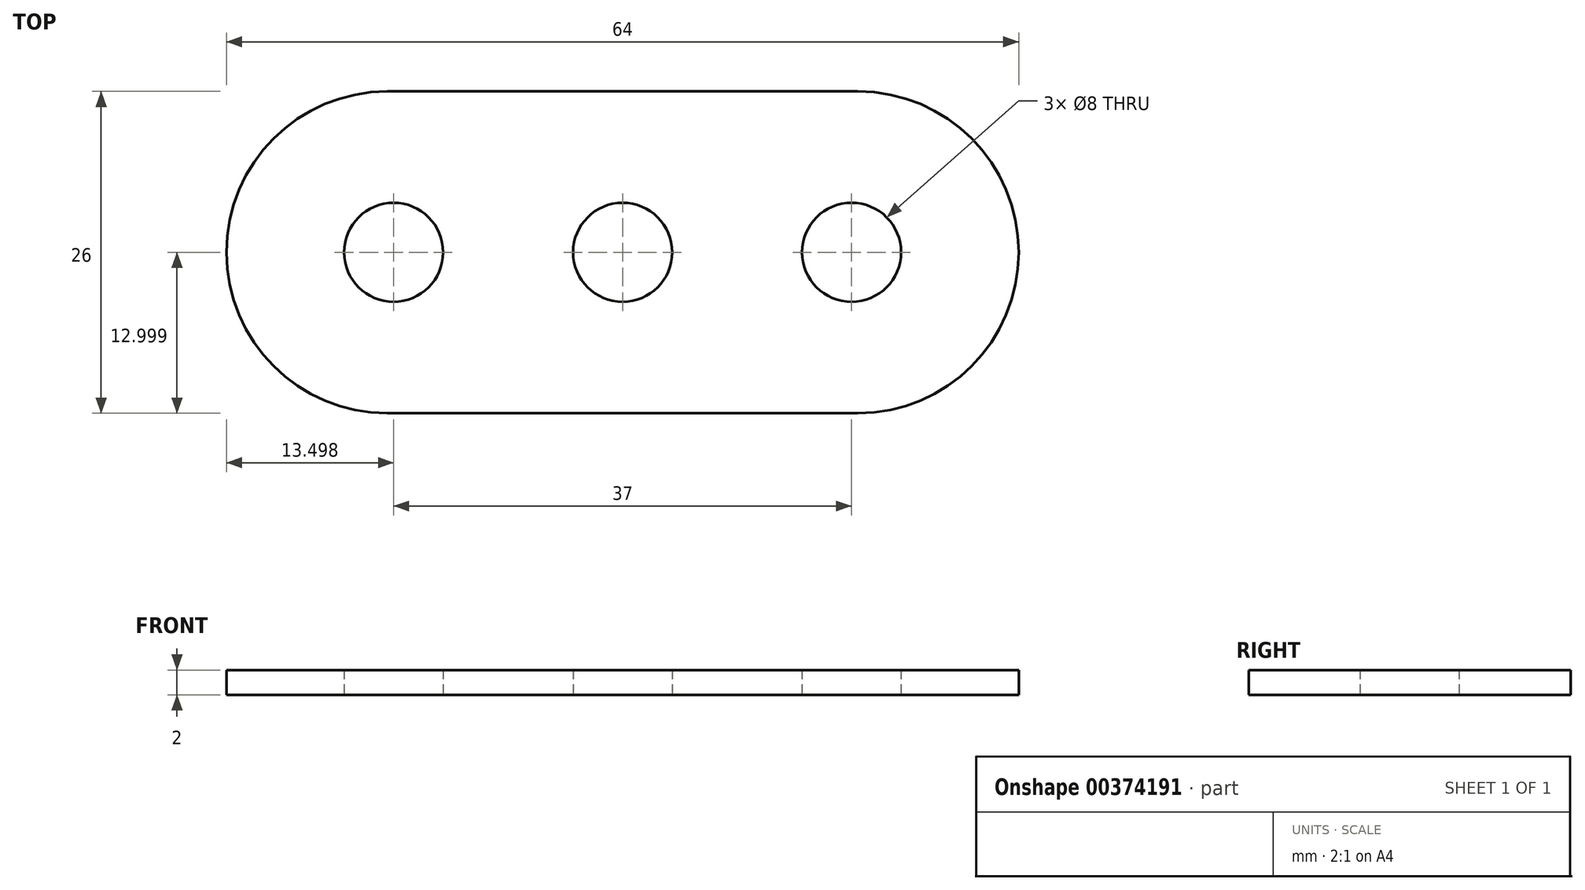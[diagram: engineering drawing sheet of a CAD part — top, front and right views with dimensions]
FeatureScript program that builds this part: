
annotation { "Feature Type Name" : "Feature", "Feature Type Description" : "" }
export const myFeature = defineFeature(function(context is Context, id is Id, definition is map)
    precondition{}
    {
        {
            var Q0;
            Q0=qCreatedBy(makeId("Top.planeOp"),FACE);
            var sketch = newSketch(context, id + "F0", { "sketchPlane" : qUnion([Q0])});
            skLineSegment(sketch, "E0.bottom", {"start": v(-21.9, 11.84) * mm, "end": v(16.1, 11.84) * mm});
            skLineSegment(sketch, "E0.top", {"start": v(-21.9, -14.16) * mm, "end": v(16.1, -14.16) * mm});
            skLineSegment(sketch, "E0.left", {"start": v(-34.9, -1.16) * mm, "end": v(-34.9, -1.16) * mm});
            skLineSegment(sketch, "E0.right", {"start": v(29.1, -1.16) * mm, "end": v(29.1, -1.16) * mm});
            skLineSegment(sketch, "E1", {"start": v(-2.9, 11.84) * mm, "end": v(-2.9, -14.16) * mm, "construction": true});
            skLineSegment(sketch, "E2", {"start": v(-34.9, -1.16) * mm, "end": v(-25.4, -1.16) * mm, "construction": true});
            skLineSegment(sketch, "E3", {"start": v(-34.9, -1.16) * mm, "end": v(29.1, -1.16) * mm, "construction": true});
            skCircle(sketch, "E4", {"center": v(-21.4, -1.16) * mm, "radius": 4 * mm});
            skCircle(sketch, "E5.MirrorC", {"center": v(15.6, -1.16) * mm, "radius": 4 * mm});
            skCircle(sketch, "E6", {"center": v(-2.9, -1.16) * mm, "radius": 4 * mm});
            skPoint(sketch, "E7.visualSharp", {"position": v(-34.9, 11.84) * mm});
            skArc(sketch, "E7.filletArc", {"start": v(-21.9, 11.84) * mm, "mid": v(-31.1, 8.03) * mm, "end": v(-34.9, -1.16) * mm});
            skPoint(sketch, "E8.visualSharp", {"position": v(-34.9, -14.16) * mm});
            skArc(sketch, "E8.filletArc", {"start": v(-34.9, -1.16) * mm, "mid": v(-31.1, -10.35) * mm, "end": v(-21.9, -14.16) * mm});
            skPoint(sketch, "E9.visualSharp", {"position": v(29.1, 11.84) * mm});
            skArc(sketch, "E9.filletArc", {"start": v(29.1, -1.16) * mm, "mid": v(25.3, 8.03) * mm, "end": v(16.1, 11.84) * mm});
            skPoint(sketch, "E10.visualSharp", {"position": v(29.1, -14.16) * mm});
            skArc(sketch, "E10.filletArc", {"start": v(16.1, -14.16) * mm, "mid": v(25.3, -10.35) * mm, "end": v(29.1, -1.16) * mm});
            skSolve(sketch);
        }
        {
            var Q0;
            Q0=makeQuery(id+"F0.imprint","IMPRINT",FACE,{"disambiguationData":[TD([[makeQuery(id+"F0.imprint","IMPRINT",EDGE,{"derivedFrom":sQuery(id+"F0.wireOp",EDGE,"E0.bottom")}),-1.0]])]});
            extrude(context, id + "F1", {"entities" : qUnion([Q0]), "depth" : 2 * mm});
        }
    });
